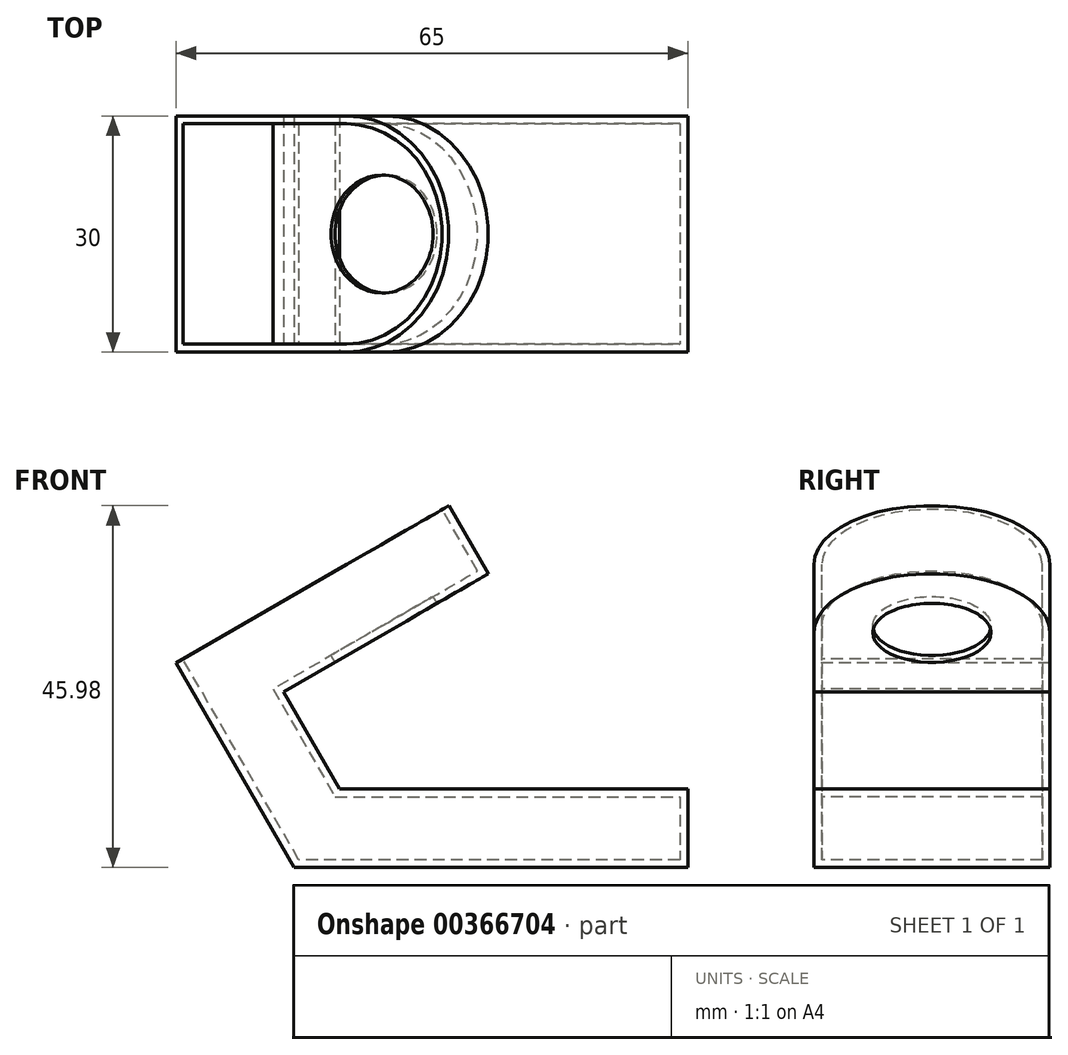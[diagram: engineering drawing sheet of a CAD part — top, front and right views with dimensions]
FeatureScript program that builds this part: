
annotation { "Feature Type Name" : "Feature", "Feature Type Description" : "" }
export const myFeature = defineFeature(function(context is Context, id is Id, definition is map)
    precondition{}
    {
        {
            var Q0;
            Q0=qCreatedBy(makeId("Front.planeOp"),FACE);
            var sketch = newSketch(context, id + "F0", { "sketchPlane" : qUnion([Q0])});
            skLineSegment(sketch, "E0", {"start": v(0, 0) * mm, "end": v(-15, 25.98) * mm});
            skLineSegment(sketch, "E1", {"start": v(-15, 25.98) * mm, "end": v(6.65, 38.48) * mm});
            skLineSegment(sketch, "E2", {"start": v(6.65, 38.48) * mm, "end": v(11.65, 29.82) * mm});
            skLineSegment(sketch, "E3", {"start": v(11.65, 29.82) * mm, "end": v(-1.34, 22.32) * mm});
            skLineSegment(sketch, "E4", {"start": v(-1.34, 22.32) * mm, "end": v(5.77, 10) * mm});
            skLineSegment(sketch, "E5", {"start": v(5.77, 10) * mm, "end": v(50, 10) * mm});
            skLineSegment(sketch, "E6", {"start": v(50, 10) * mm, "end": v(50, 0) * mm});
            skLineSegment(sketch, "E7", {"start": v(50, 0) * mm, "end": v(0, 0) * mm});
            skSolve(sketch);
        }
        {
            var Q0;
            Q0 = qSketchRegion(id + "F0", true);
            extrude(context, id + "F1", {"entities" : qUnion([Q0]), "endBound" : BoundingType.SYMMETRIC, "oppositeDirection" : true, "depth" : 30 * mm});
        }
        {
            var Q0;
            Q0=makeQuery(id+"F1.opExtrude","SWEPT_FACE",FACE,{"disambiguationData":[OSD([sQuery(id+"F0.wireOp",EDGE,"E1")])]});
            var sketch = newSketch(context, id + "F2", { "sketchPlane" : qUnion([Q0])});
            skArc(sketch, "E8", {"start": v(25, -15) * mm, "mid": v(40, 0) * mm, "end": v(25, 15) * mm});
            skSolve(sketch);
        }
        {
            var Q0;
            Q0=makeQuery(id+"F2.imprint","IMPRINT",FACE,{"disambiguationData":[TD([[makeQuery(id+"F2.imprint","IMPRINT",EDGE,{"derivedFrom":sQuery(id+"F2.wireOp",EDGE,"E8")}),1.0]])]});
            extrude(context, id + "F3", {"entities" : qUnion([Q0]), "operationType" : NewBodyOperationType.ADD, "oppositeDirection" : true, "depth" : 10 * mm});
        }
        {
            var Q0;
            {var subQ0=sQuery(id+"F0.wireOp",EDGE,"E1");Q0=makeQuery(id+"F3.boolean.opBoolean","MERGE",FACE,{"derivedFrom":[makeQuery(id+"F1.opExtrude","SWEPT_FACE",FACE,{"disambiguationData":[OSD([subQ0])]}),makeQuery(id+"F3.opExtrude","CAP_FACE",FACE,{"disambiguationData":[OSD([subQ0,sQuery(id+"F0.wireOp",EDGE,"E2"),sQuery(id+"F2.wireOp",EDGE,"E8")])],"isStart":true})]});}
            shell(context, id + "F4", {"entities" : qUnion([Q0]), "thickness" : 1 * mm});
        }
        {
            var Q0;
            Q0=makeQuery(id+"F4.opShell","OFFSET_FACE",FACE,{"disambiguationData":[OSD([sQuery(id+"F0.wireOp",EDGE,"E1"),sQuery(id+"F0.wireOp",EDGE,"E2"),sQuery(id+"F0.wireOp",EDGE,"E3"),sQuery(id+"F2.wireOp",EDGE,"E8")])]});
            var sketch = newSketch(context, id + "F5", { "sketchPlane" : qUnion([Q0])});
            skPoint(sketch, "E9", {"position": v(25, 0) * mm});
            skCircle(sketch, "E10", {"center": v(25, 0) * mm, "radius": 7.5 * mm});
            skSolve(sketch);
        }
        {
            var Q0;
            Q0 = qSketchRegion(id + "F5", true);
            extrude(context, id + "F6", {"entities" : qUnion([Q0]), "operationType" : NewBodyOperationType.REMOVE, "oppositeDirection" : true, "depth" : 10 * mm});
        }
    });
